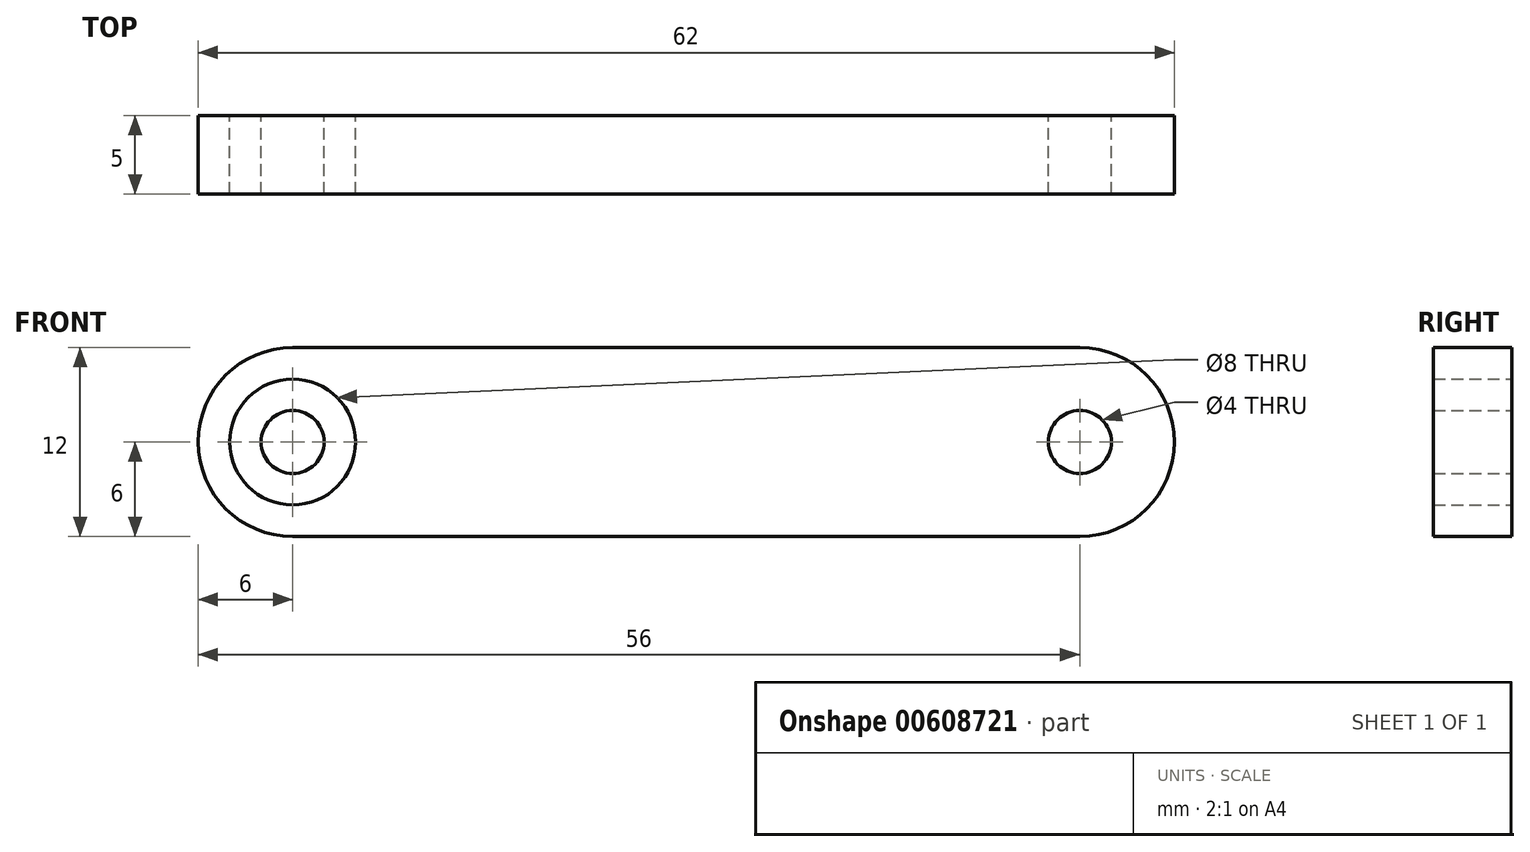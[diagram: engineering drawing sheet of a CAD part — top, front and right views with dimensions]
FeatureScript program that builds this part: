
annotation { "Feature Type Name" : "Feature", "Feature Type Description" : "" }
export const myFeature = defineFeature(function(context is Context, id is Id, definition is map)
    precondition{}
    {
        {
            var Q0;
            Q0=qCreatedBy(makeId("Front.planeOp"),FACE);
            var sketch = newSketch(context, id + "F0", { "sketchPlane" : qUnion([Q0])});
            skCircle(sketch, "E0", {"center": v(-25, 0) * mm, "radius": 2 * mm});
            skCircle(sketch, "E1", {"center": v(-25, 0) * mm, "radius": 4 * mm});
            skArc(sketch, "E2", {"start": v(-25, 6) * mm, "mid": v(-31, 0) * mm, "end": v(-25, -6) * mm});
            skLineSegment(sketch, "E3", {"start": v(0, 6) * mm, "end": v(0, -6) * mm, "construction": true});
            skLineSegment(sketch, "E4", {"start": v(-25, -6) * mm, "end": v(0, -6) * mm});
            skLineSegment(sketch, "E5", {"start": v(-25, 6) * mm, "end": v(0, 6) * mm});
            skCircle(sketch, "E6.MirrorC", {"center": v(25, 0) * mm, "radius": 2 * mm});
            skArc(sketch, "E7.MirrorC", {"start": v(25, 6) * mm, "mid": v(31, 0) * mm, "end": v(25, -6) * mm});
            skLineSegment(sketch, "E8.MirrorCS", {"start": v(25, -6) * mm, "end": v(0, -6) * mm});
            skLineSegment(sketch, "E9.MirrorCS", {"start": v(25, 6) * mm, "end": v(0, 6) * mm});
            skCircle(sketch, "E10.MirrorC", {"center": v(25, 0) * mm, "radius": 4 * mm});
            skSolve(sketch);
        }
        {
            var Q0;
            Q0=makeQuery(id+"F0.imprint","IMPRINT",FACE,{"disambiguationData":[TD([[makeQuery(id+"F0.imprint","IMPRINT",EDGE,{"derivedFrom":sQuery(id+"F0.wireOp",EDGE,"E1")}),-1.0]])]});
            var Q1;
            Q1=makeQuery(id+"F0.imprint","IMPRINT",FACE,{"disambiguationData":[TD([[makeQuery(id+"F0.imprint","IMPRINT",EDGE,{"derivedFrom":sQuery(id+"F0.wireOp",EDGE,"E6.MirrorC")}),-1.0]])]});
            var Q2;
            Q2=makeQuery(id+"F0.imprint","IMPRINT",FACE,{"disambiguationData":[TD([[makeQuery(id+"F0.imprint","IMPRINT",EDGE,{"derivedFrom":sQuery(id+"F0.wireOp",EDGE,"E0")}),1.0]])]});
            extrude(context, id + "F1", {"entities" : qUnion([Q0, Q1, Q2]), "depth" : 5 * mm, "offsetDistance" : 25 * mm});
        }
    });
